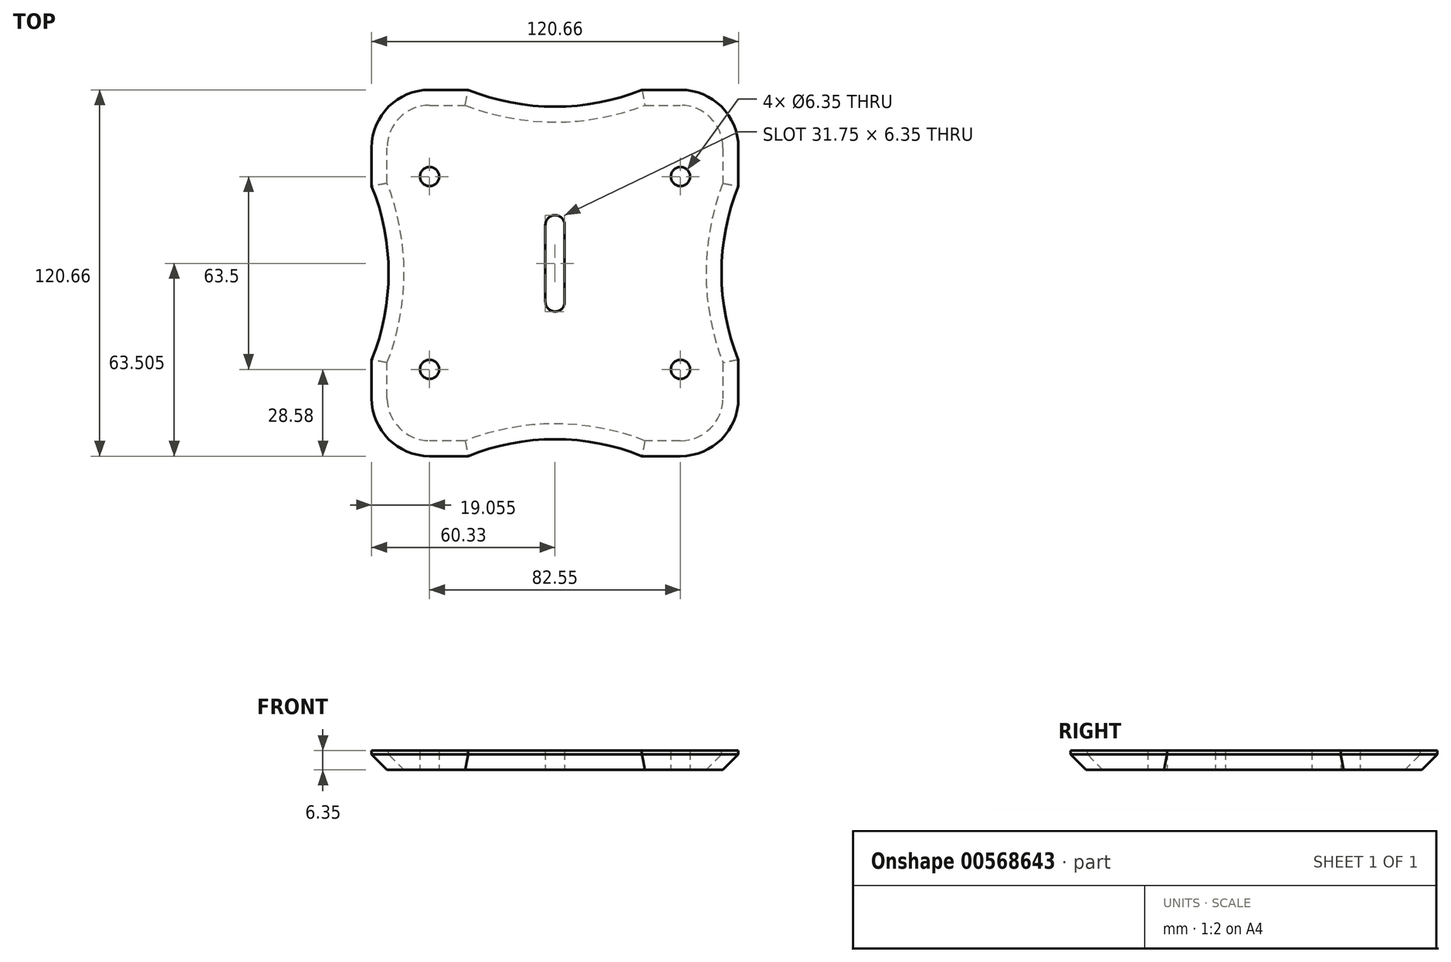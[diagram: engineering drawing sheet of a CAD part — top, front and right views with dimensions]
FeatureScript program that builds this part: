
annotation { "Feature Type Name" : "Feature", "Feature Type Description" : "" }
export const myFeature = defineFeature(function(context is Context, id is Id, definition is map)
    precondition{}
    {
        {
            var Q0;
            Q0=qCreatedBy(makeId("Top.planeOp"),FACE);
            var sketch = newSketch(context, id + "F0", { "sketchPlane" : qUnion([Q0])});
            skLineSegment(sketch, "E0.bottom", {"start": v(60.32, -60.32) * mm, "end": v(-60.33, -60.33) * mm});
            skLineSegment(sketch, "E0.top", {"start": v(60.33, 60.32) * mm, "end": v(-60.33, 60.32) * mm});
            skLineSegment(sketch, "E0.left", {"start": v(60.32, -60.32) * mm, "end": v(60.33, 60.33) * mm});
            skLineSegment(sketch, "E0.right", {"start": v(-60.33, -60.33) * mm, "end": v(-60.33, 60.32) * mm});
            skPoint(sketch, "E0.middle", {"position": v(0, 0) * mm});
            skCircle(sketch, "E1", {"center": v(41.27, 31.75) * mm, "radius": 3.18 * mm});
            skCircle(sketch, "E2", {"center": v(41.27, -31.75) * mm, "radius": 3.18 * mm});
            skCircle(sketch, "E3", {"center": v(-41.28, -31.75) * mm, "radius": 3.18 * mm});
            skCircle(sketch, "E4", {"center": v(-41.28, 31.75) * mm, "radius": 3.18 * mm});
            skSolve(sketch);
        }
        {
            var Q0;
            Q0 = qSketchRegion(id + "F0", true);
            extrude(context, id + "F1", {"entities" : qUnion([Q0]), "depth" : 6.35 * mm, "offsetDistance" : 25.4 * mm});
        }
        {
            var Q0;
            Q0=makeQuery(id+"F1.opExtrude","CAP_FACE",FACE,{"disambiguationData":[OSD([sQuery(id+"F0.wireOp",EDGE,"E0.bottom"),sQuery(id+"F0.wireOp",EDGE,"E0.top"),sQuery(id+"F0.wireOp",EDGE,"E0.left"),sQuery(id+"F0.wireOp",EDGE,"E0.right"),sQuery(id+"F0.wireOp",EDGE,"E1"),sQuery(id+"F0.wireOp",EDGE,"E2"),sQuery(id+"F0.wireOp",EDGE,"E3"),sQuery(id+"F0.wireOp",EDGE,"E4")])],"isStart":true});
            var sketch = newSketch(context, id + "F2", { "sketchPlane" : qUnion([Q0])});
            skCircle(sketch, "E5", {"center": v(0, -15.88) * mm, "radius": 3.18 * mm});
            skCircle(sketch, "E6", {"center": v(0, 9.53) * mm, "radius": 3.18 * mm});
            skLineSegment(sketch, "E7", {"start": v(-3.18, -15.88) * mm, "end": v(-3.17, 9.52) * mm});
            skLineSegment(sketch, "E8", {"start": v(3.17, 9.68) * mm, "end": v(3.18, -15.88) * mm});
            skSolve(sketch);
        }
        {
            var Q0;
            Q0 = qSketchRegion(id + "F2", true);
            extrude(context, id + "F3", {"entities" : qUnion([Q0]), "operationType" : NewBodyOperationType.REMOVE, "oppositeDirection" : true, "depth" : 25.4 * mm, "offsetDistance" : 25.4 * mm});
        }
        {
            var Q0;
            Q0 = qSketchRegion(id + "F2", true);
            extrude(context, id + "F4", {"entities" : qUnion([Q0]), "operationType" : NewBodyOperationType.REMOVE, "oppositeDirection" : true, "depth" : 25.4 * mm, "offsetDistance" : 25.4 * mm});
        }
        {
            var Q0;
            Q0=makeQuery(id+"F1.opExtrude","CAP_FACE",FACE,{"disambiguationData":[OSD([sQuery(id+"F0.wireOp",EDGE,"E0.bottom"),sQuery(id+"F0.wireOp",EDGE,"E0.top"),sQuery(id+"F0.wireOp",EDGE,"E0.left"),sQuery(id+"F0.wireOp",EDGE,"E0.right"),sQuery(id+"F0.wireOp",EDGE,"E1"),sQuery(id+"F0.wireOp",EDGE,"E2"),sQuery(id+"F0.wireOp",EDGE,"E3"),sQuery(id+"F0.wireOp",EDGE,"E4")])],"isStart":false});
            var sketch = newSketch(context, id + "F5", { "sketchPlane" : qUnion([Q0])});
            skLineSegment(sketch, "E9.bottom", {"start": v(41.28, 60.33) * mm, "end": v(-41.28, 60.33) * mm});
            skLineSegment(sketch, "E9.top", {"start": v(41.28, -60.33) * mm, "end": v(-41.28, -60.33) * mm});
            skLineSegment(sketch, "E9.left", {"start": v(60.33, 41.28) * mm, "end": v(60.33, -41.28) * mm});
            skLineSegment(sketch, "E9.right", {"start": v(-60.33, 41.28) * mm, "end": v(-60.33, -41.28) * mm});
            skPoint(sketch, "E10.visualSharp", {"position": v(60.33, 60.33) * mm});
            skArc(sketch, "E10.filletArc", {"start": v(60.33, 41.28) * mm, "mid": v(54.75, 54.75) * mm, "end": v(41.28, 60.33) * mm});
            skPoint(sketch, "E11.visualSharp", {"position": v(60.33, -60.33) * mm});
            skArc(sketch, "E11.filletArc", {"start": v(41.28, -60.33) * mm, "mid": v(54.75, -54.75) * mm, "end": v(60.33, -41.28) * mm});
            skPoint(sketch, "E12.visualSharp", {"position": v(-60.33, -60.33) * mm});
            skArc(sketch, "E12.filletArc", {"start": v(-60.33, -41.28) * mm, "mid": v(-54.75, -54.75) * mm, "end": v(-41.28, -60.33) * mm});
            skPoint(sketch, "E13.visualSharp", {"position": v(-60.33, 60.33) * mm});
            skArc(sketch, "E13.filletArc", {"start": v(-41.28, 60.33) * mm, "mid": v(-54.75, 54.75) * mm, "end": v(-60.33, 41.28) * mm});
            skLineSegment(sketch, "E14", {"start": v(60.33, 41.28) * mm, "end": v(60.33, 28.58) * mm});
            skLineSegment(sketch, "E15", {"start": v(60.33, -41.28) * mm, "end": v(60.33, -28.57) * mm});
            skArc(sketch, "E16", {"start": v(60.32, 28.57) * mm, "mid": v(54.76, 0) * mm, "end": v(60.32, -28.57) * mm});
            skLineSegment(sketch, "E17", {"start": v(-60.33, 41.28) * mm, "end": v(-60.33, 28.57) * mm});
            skLineSegment(sketch, "E18", {"start": v(-60.33, -41.28) * mm, "end": v(-60.33, -28.58) * mm});
            skArc(sketch, "E19", {"start": v(-60.33, -28.58) * mm, "mid": v(-54.76, 0) * mm, "end": v(-60.33, 28.57) * mm});
            skLineSegment(sketch, "E20", {"start": v(41.28, -60.33) * mm, "end": v(28.58, -60.32) * mm});
            skLineSegment(sketch, "E21", {"start": v(-41.28, -60.33) * mm, "end": v(-28.57, -60.33) * mm});
            skLineSegment(sketch, "E22", {"start": v(41.28, 60.33) * mm, "end": v(28.57, 60.32) * mm});
            skLineSegment(sketch, "E23", {"start": v(-41.28, 60.33) * mm, "end": v(-28.58, 60.32) * mm});
            skArc(sketch, "E24", {"start": v(-28.58, 60.32) * mm, "mid": v(0, 54.76) * mm, "end": v(28.57, 60.32) * mm});
            skArc(sketch, "E25", {"start": v(28.57, -60.32) * mm, "mid": v(0, -54.76) * mm, "end": v(-28.57, -60.32) * mm});
            skSolve(sketch);
        }
        {
            var Q0;
            Q0=makeQuery(id+"F5.imprint","IMPRINT",FACE,{"disambiguationData":[TD([[makeQuery(id+"F5.imprint","IMPRINT",EDGE,{"derivedFrom":sQuery(id+"F5.wireOp",EDGE,"E9.bottom")}),1.0]])]});
            var Q1;
            Q1=makeQuery(id+"F5.imprint","IMPRINT",FACE,{"disambiguationData":[TD([[makeQuery(id+"F5.imprint","IMPRINT",EDGE,{"derivedFrom":sQuery(id+"F5.wireOp",EDGE,"E9.top")}),-1.0]])]});
            var Q2;
            Q2=makeQuery(id+"F5.imprint","IMPRINT",FACE,{"disambiguationData":[TD([[makeQuery(id+"F5.imprint","IMPRINT",EDGE,{"derivedFrom":sQuery(id+"F5.wireOp",EDGE,"E9.left")}),1.0]])]});
            var Q3;
            Q3=makeQuery(id+"F5.imprint","IMPRINT",FACE,{"disambiguationData":[TD([[makeQuery(id+"F5.imprint","IMPRINT",EDGE,{"derivedFrom":sQuery(id+"F5.wireOp",EDGE,"E9.right")}),-1.0]])]});
            var Q4;
            Q4=makeQuery(id+"F5.imprint","IMPRINT",FACE,{"disambiguationData":[TD([[makeQuery(id+"F5.imprint","IMPRINT",EDGE,{"derivedFrom":makeQuery(id+"F1.opExtrude","CAP_EDGE",EDGE,{"disambiguationData":[OSD([sQuery(id+"F0.wireOp",EDGE,"E1")])],"isStart":false})}),1.0]])]});
            var Q5;
            Q5=makeQuery(id+"F5.imprint","IMPRINT",FACE,{"disambiguationData":[TD([[makeQuery(id+"F5.imprint","IMPRINT",EDGE,{"derivedFrom":makeQuery(id+"F1.opExtrude","CAP_EDGE",EDGE,{"disambiguationData":[OSD([sQuery(id+"F0.wireOp",EDGE,"E2")])],"isStart":false})}),1.0]])]});
            var Q6;
            Q6=makeQuery(id+"F5.imprint","IMPRINT",FACE,{"disambiguationData":[TD([[makeQuery(id+"F5.imprint","IMPRINT",EDGE,{"derivedFrom":makeQuery(id+"F1.opExtrude","CAP_EDGE",EDGE,{"disambiguationData":[OSD([sQuery(id+"F0.wireOp",EDGE,"E3")])],"isStart":false})}),1.0]])]});
            var Q7;
            Q7=makeQuery(id+"F5.imprint","IMPRINT",FACE,{"disambiguationData":[TD([[makeQuery(id+"F5.imprint","IMPRINT",EDGE,{"derivedFrom":makeQuery(id+"F1.opExtrude","CAP_EDGE",EDGE,{"disambiguationData":[OSD([sQuery(id+"F0.wireOp",EDGE,"E4")])],"isStart":false})}),1.0]])]});
            var Q8;
            {var subQ0=makeQuery(id+"F1.opExtrude","CAP_FACE",FACE,{"disambiguationData":[OSD([sQuery(id+"F0.wireOp",EDGE,"E0.bottom"),sQuery(id+"F0.wireOp",EDGE,"E0.top"),sQuery(id+"F0.wireOp",EDGE,"E0.left"),sQuery(id+"F0.wireOp",EDGE,"E0.right"),sQuery(id+"F0.wireOp",EDGE,"E1"),sQuery(id+"F0.wireOp",EDGE,"E2"),sQuery(id+"F0.wireOp",EDGE,"E3"),sQuery(id+"F0.wireOp",EDGE,"E4")])],"isStart":false});Q8=makeQuery(id+"F5.imprint","IMPRINT",FACE,{"disambiguationData":[TD([[makeQuery(id+"F5.imprint","IMPRINT",EDGE,{"derivedFrom":makeQuery(id+"F3.boolean.opBoolean","INTERSECT",EDGE,{"derivedFrom":[subQ0,makeQuery(id+"F3.opExtrude","SWEPT_FACE",FACE,{"disambiguationData":[OSD([sQuery(id+"F2.wireOp",EDGE,"E5")])]})]})}),1.0]])]});}
            var Q9;
            {var subQ0=sQuery(id+"F5.wireOp",EDGE,"E10.filletArc");Q9=makeQuery(id+"F5.imprint","IMPRINT",FACE,{"disambiguationData":[TD([[makeQuery(id+"F5.imprint","IMPRINT",EDGE,{"derivedFrom":subQ0}),-1.0]])]});}
            var Q10;
            {var subQ0=sQuery(id+"F5.wireOp",EDGE,"E12.filletArc");Q10=makeQuery(id+"F5.imprint","IMPRINT",FACE,{"disambiguationData":[TD([[makeQuery(id+"F5.imprint","IMPRINT",EDGE,{"derivedFrom":subQ0}),-1.0]])]});}
            var Q11;
            {var subQ0=sQuery(id+"F5.wireOp",EDGE,"E13.filletArc");Q11=makeQuery(id+"F5.imprint","IMPRINT",FACE,{"disambiguationData":[TD([[makeQuery(id+"F5.imprint","IMPRINT",EDGE,{"derivedFrom":subQ0}),-1.0]])]});}
            var Q12;
            {var subQ0=sQuery(id+"F5.wireOp",EDGE,"E11.filletArc");Q12=makeQuery(id+"F5.imprint","IMPRINT",FACE,{"disambiguationData":[TD([[makeQuery(id+"F5.imprint","IMPRINT",EDGE,{"derivedFrom":subQ0}),-1.0]])]});}
            extrude(context, id + "F6", {"entities" : qUnion([Q0, Q1, Q2, Q3, Q4, Q5, Q6, Q7, Q8, Q9, Q10, Q11, Q12]), "operationType" : NewBodyOperationType.REMOVE, "oppositeDirection" : true, "depth" : 25.4 * mm, "offsetDistance" : 25.4 * mm});
        }
        {
            var Q0;
            Q0=makeQuery(id+"F6.boolean.opBoolean","INTERSECT",EDGE,{"derivedFrom":[makeQuery(id+"F1.opExtrude","CAP_FACE",FACE,{"disambiguationData":[OSD([sQuery(id+"F0.wireOp",EDGE,"E0.bottom"),sQuery(id+"F0.wireOp",EDGE,"E0.top"),sQuery(id+"F0.wireOp",EDGE,"E0.left"),sQuery(id+"F0.wireOp",EDGE,"E0.right"),sQuery(id+"F0.wireOp",EDGE,"E1"),sQuery(id+"F0.wireOp",EDGE,"E2"),sQuery(id+"F0.wireOp",EDGE,"E3"),sQuery(id+"F0.wireOp",EDGE,"E4")])],"isStart":true}),makeQuery(id+"F6.opExtrude","SWEPT_FACE",FACE,{"disambiguationData":[OSD([sQuery(id+"F5.wireOp",EDGE,"E24")])]})]});
            var Q1;
            Q1=makeQuery(id+"F6.boolean.opBoolean","INTERSECT",EDGE,{"derivedFrom":[makeQuery(id+"F1.opExtrude","CAP_FACE",FACE,{"disambiguationData":[OSD([sQuery(id+"F0.wireOp",EDGE,"E0.bottom"),sQuery(id+"F0.wireOp",EDGE,"E0.top"),sQuery(id+"F0.wireOp",EDGE,"E0.left"),sQuery(id+"F0.wireOp",EDGE,"E0.right"),sQuery(id+"F0.wireOp",EDGE,"E1"),sQuery(id+"F0.wireOp",EDGE,"E2"),sQuery(id+"F0.wireOp",EDGE,"E3"),sQuery(id+"F0.wireOp",EDGE,"E4")])],"isStart":true}),makeQuery(id+"F6.opExtrude","SWEPT_FACE",FACE,{"disambiguationData":[OSD([sQuery(id+"F5.wireOp",EDGE,"E10.filletArc")])]})]});
            var Q2;
            Q2=makeQuery(id+"F6.boolean.opBoolean","INTERSECT",EDGE,{"derivedFrom":[makeQuery(id+"F1.opExtrude","CAP_FACE",FACE,{"disambiguationData":[OSD([sQuery(id+"F0.wireOp",EDGE,"E0.bottom"),sQuery(id+"F0.wireOp",EDGE,"E0.top"),sQuery(id+"F0.wireOp",EDGE,"E0.left"),sQuery(id+"F0.wireOp",EDGE,"E0.right"),sQuery(id+"F0.wireOp",EDGE,"E1"),sQuery(id+"F0.wireOp",EDGE,"E2"),sQuery(id+"F0.wireOp",EDGE,"E3"),sQuery(id+"F0.wireOp",EDGE,"E4")])],"isStart":true}),makeQuery(id+"F6.opExtrude","SWEPT_FACE",FACE,{"disambiguationData":[OSD([sQuery(id+"F5.wireOp",EDGE,"E16")])]})]});
            var Q3;
            Q3=makeQuery(id+"F6.boolean.opBoolean","INTERSECT",EDGE,{"derivedFrom":[makeQuery(id+"F1.opExtrude","CAP_FACE",FACE,{"disambiguationData":[OSD([sQuery(id+"F0.wireOp",EDGE,"E0.bottom"),sQuery(id+"F0.wireOp",EDGE,"E0.top"),sQuery(id+"F0.wireOp",EDGE,"E0.left"),sQuery(id+"F0.wireOp",EDGE,"E0.right"),sQuery(id+"F0.wireOp",EDGE,"E1"),sQuery(id+"F0.wireOp",EDGE,"E2"),sQuery(id+"F0.wireOp",EDGE,"E3"),sQuery(id+"F0.wireOp",EDGE,"E4")])],"isStart":true}),makeQuery(id+"F6.opExtrude","SWEPT_FACE",FACE,{"disambiguationData":[OSD([sQuery(id+"F5.wireOp",EDGE,"E11.filletArc")])]})]});
            var Q4;
            {var subQ0=sQuery(id+"F0.wireOp",EDGE,"E0.bottom");Q4=makeQuery(id+"F6.boolean.opBoolean","SPLIT",EDGE,{"disambiguationData":[TD([makeQuery(id+"F6.opExtrude","SWEPT_FACE",FACE,{"disambiguationData":[OSD([sQuery(id+"F5.wireOp",EDGE,"E12.filletArc")])]})])],"derivedFrom":makeQuery(id+"F1.opExtrude","CAP_EDGE",EDGE,{"disambiguationData":[OSD([subQ0])],"isStart":true})});}
            var Q5;
            Q5=makeQuery(id+"F6.boolean.opBoolean","INTERSECT",EDGE,{"derivedFrom":[makeQuery(id+"F1.opExtrude","CAP_FACE",FACE,{"disambiguationData":[OSD([sQuery(id+"F0.wireOp",EDGE,"E0.bottom"),sQuery(id+"F0.wireOp",EDGE,"E0.top"),sQuery(id+"F0.wireOp",EDGE,"E0.left"),sQuery(id+"F0.wireOp",EDGE,"E0.right"),sQuery(id+"F0.wireOp",EDGE,"E1"),sQuery(id+"F0.wireOp",EDGE,"E2"),sQuery(id+"F0.wireOp",EDGE,"E3"),sQuery(id+"F0.wireOp",EDGE,"E4")])],"isStart":true}),makeQuery(id+"F6.opExtrude","SWEPT_FACE",FACE,{"disambiguationData":[OSD([sQuery(id+"F5.wireOp",EDGE,"E25")])]})]});
            var Q6;
            Q6=makeQuery(id+"F6.boolean.opBoolean","INTERSECT",EDGE,{"derivedFrom":[makeQuery(id+"F1.opExtrude","CAP_FACE",FACE,{"disambiguationData":[OSD([sQuery(id+"F0.wireOp",EDGE,"E0.bottom"),sQuery(id+"F0.wireOp",EDGE,"E0.top"),sQuery(id+"F0.wireOp",EDGE,"E0.left"),sQuery(id+"F0.wireOp",EDGE,"E0.right"),sQuery(id+"F0.wireOp",EDGE,"E1"),sQuery(id+"F0.wireOp",EDGE,"E2"),sQuery(id+"F0.wireOp",EDGE,"E3"),sQuery(id+"F0.wireOp",EDGE,"E4")])],"isStart":true}),makeQuery(id+"F6.opExtrude","SWEPT_FACE",FACE,{"disambiguationData":[OSD([sQuery(id+"F5.wireOp",EDGE,"E13.filletArc")])]})]});
            var Q7;
            {var subQ0=sQuery(id+"F0.wireOp",EDGE,"E0.right");Q7=makeQuery(id+"F6.boolean.opBoolean","SPLIT",EDGE,{"disambiguationData":[TD([makeQuery(id+"F6.opExtrude","SWEPT_FACE",FACE,{"disambiguationData":[OSD([sQuery(id+"F5.wireOp",EDGE,"E13.filletArc")])]})])],"derivedFrom":makeQuery(id+"F1.opExtrude","CAP_EDGE",EDGE,{"disambiguationData":[OSD([subQ0])],"isStart":true})});}
            var Q8;
            Q8=makeQuery(id+"F6.boolean.opBoolean","INTERSECT",EDGE,{"derivedFrom":[makeQuery(id+"F1.opExtrude","CAP_FACE",FACE,{"disambiguationData":[OSD([sQuery(id+"F0.wireOp",EDGE,"E0.bottom"),sQuery(id+"F0.wireOp",EDGE,"E0.top"),sQuery(id+"F0.wireOp",EDGE,"E0.left"),sQuery(id+"F0.wireOp",EDGE,"E0.right"),sQuery(id+"F0.wireOp",EDGE,"E1"),sQuery(id+"F0.wireOp",EDGE,"E2"),sQuery(id+"F0.wireOp",EDGE,"E3"),sQuery(id+"F0.wireOp",EDGE,"E4")])],"isStart":true}),makeQuery(id+"F6.opExtrude","SWEPT_FACE",FACE,{"disambiguationData":[OSD([sQuery(id+"F5.wireOp",EDGE,"E19")])]})]});
            chamfer(context, id + "F7", {"entities" : qUnion([Q0, Q1, Q2, Q3, Q4, Q5, Q6, Q7, Q8]), "width" : 5.08 * mm, "tangentPropagation" : true});
        }
    });
